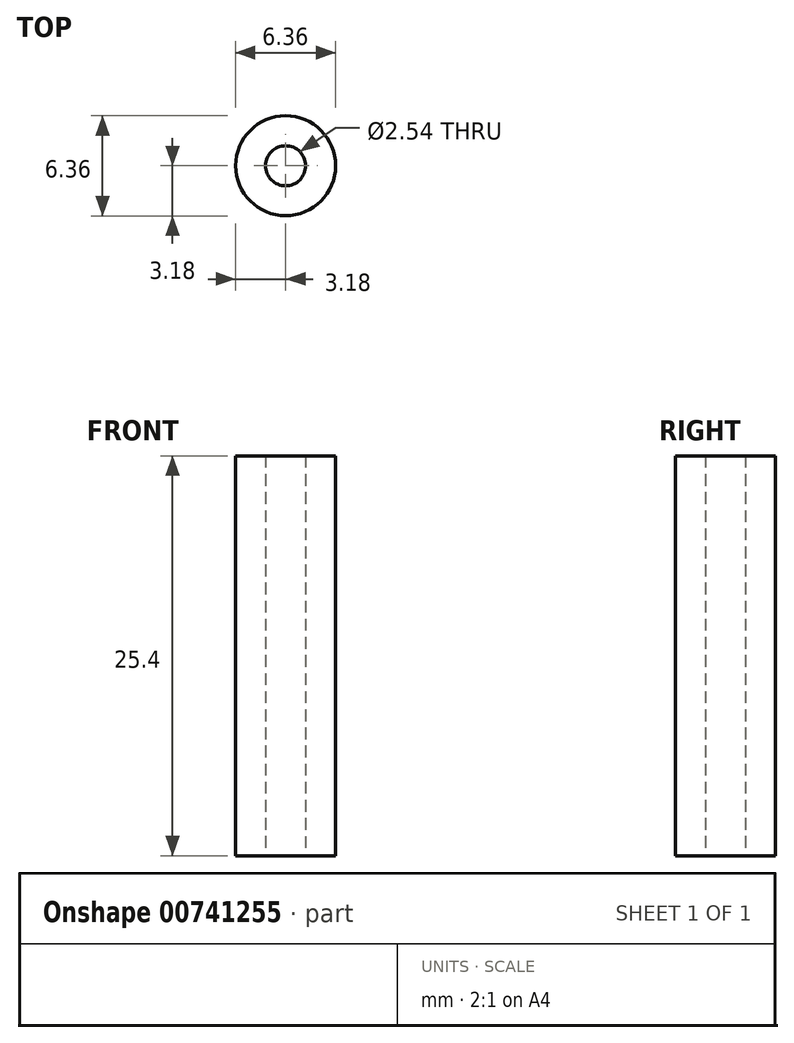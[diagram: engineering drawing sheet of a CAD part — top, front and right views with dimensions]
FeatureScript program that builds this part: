
annotation { "Feature Type Name" : "Feature", "Feature Type Description" : "" }
export const myFeature = defineFeature(function(context is Context, id is Id, definition is map)
    precondition{}
    {
        {
            var Q0;
            Q0=qCreatedBy(makeId("Top.planeOp"),FACE);
            var sketch = newSketch(context, id + "F0", { "sketchPlane" : qUnion([Q0])});
            skCircle(sketch, "E0", {"center": v(0, 0) * mm, "radius": 3.18 * mm});
            skCircle(sketch, "E1", {"center": v(0, 0) * mm, "radius": 1.27 * mm});
            skSolve(sketch);
        }
        {
            var Q0;
            Q0=makeQuery(id+"F0.imprint","IMPRINT",FACE,{"disambiguationData":[TD([[makeQuery(id+"F0.imprint","IMPRINT",EDGE,{"derivedFrom":sQuery(id+"F0.wireOp",EDGE,"E0")}),1.0]])]});
            extrude(context, id + "F1", {"entities" : qUnion([Q0]), "depth" : 25.4 * mm, "offsetDistance" : 25.4 * mm});
        }
    });
